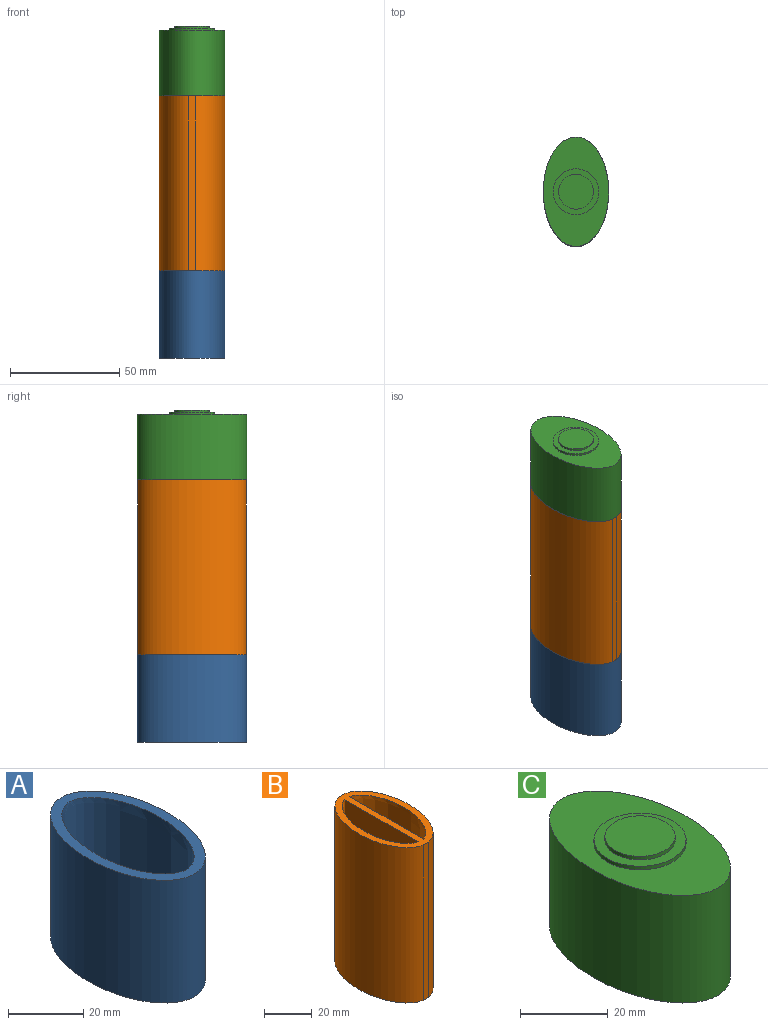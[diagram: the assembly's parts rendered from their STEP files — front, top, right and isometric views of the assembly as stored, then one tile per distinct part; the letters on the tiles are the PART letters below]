
ASSEMBLY  parts=3 mates=2
PART A: 5 faces, bbox 30x50x40 mm
  f0: plane 50x30mm, normal (0,0,-1), area 1178.1mm2, adj f2
  f1: extruded ~44x37mm, area 4018.9mm2, adj f3,f4
  f2: extruded ~50x40mm, area 5105.4mm2, adj f0,f3
  f3: plane 50x30mm, normal (0,0,1), area 354.7mm2, adj f1,f2
  f4: plane 44x24mm, normal (0,0,1), area 823.4mm2, adj f1
PART B: 10 faces, bbox 30x49.7x80 mm
  f0: plane 80x3mm, normal (0,1,0), area 240mm2, adj f1,f7,f8,f9
  f1: extruded ~80x49.75mm, area 4864.3mm2, adj f0,f2,f8,f9
  f2: plane 80x3mm, normal (0,-1,0), area 240mm2, adj f1,f7,f8,f9
  f3: plane 80x43.62mm, normal (1,0,0), area 3490mm2, adj f5,f8,f9
  f4: extruded ~80x43.62mm, area 4107.5mm2, adj f6,f8,f9
  f5: extruded ~80x43.62mm, area 4107.5mm2, adj f3,f8,f9
  f6: plane 80x43.62mm, normal (-1,0,0), area 3490mm2, adj f4,f8,f9
  f7: extruded ~80x49.75mm, area 4864.3mm2, adj f0,f2,f8,f9
  f8: plane 49.75x30mm, normal (0,0,1), area 485.8mm2, adj f0,f1,f2,f3,f4,f5,f6,f7
  f9: plane 49.75x30mm, normal (0,0,-1), area 485.8mm2, adj f0,f1,f2,f3,f4,f5,f6,f7
PART C: 7 faces, bbox 30x50x32 mm
  f0: extruded ~50x30mm, area 3829.1mm2, adj f1,f2
  f1: plane 50x30mm, normal (0,0,1), area 831.7mm2, adj f0,f3
  f2: plane 50x30mm, normal (0,0,-1), area 1178.1mm2, adj f0
  f3: cylinder r=10.5mm len=21mm, axis (0,0,-1), area 66mm2, adj f1,f4
  f4: plane 21x21mm, normal (0,0,1), area 145.3mm2, adj f3,f6
  f5: plane 16x16mm, normal (0,0,1), area 201.1mm2, adj f6
  f6: cylinder r=8mm len=16mm, axis (0,0,-1), area 50.3mm2, adj f4,f5
PLACE A at identity
PLACE B t=(0,0,40)mm
PLACE C t=(0,0,120)mm
MATE fastened B.f9 <-> A.f3  axis (0,0,-1) through (0,0,40)mm
MATE fastened C.f6 <-> B.f8  axis (0,0,-1) through (0,0,120)mm
